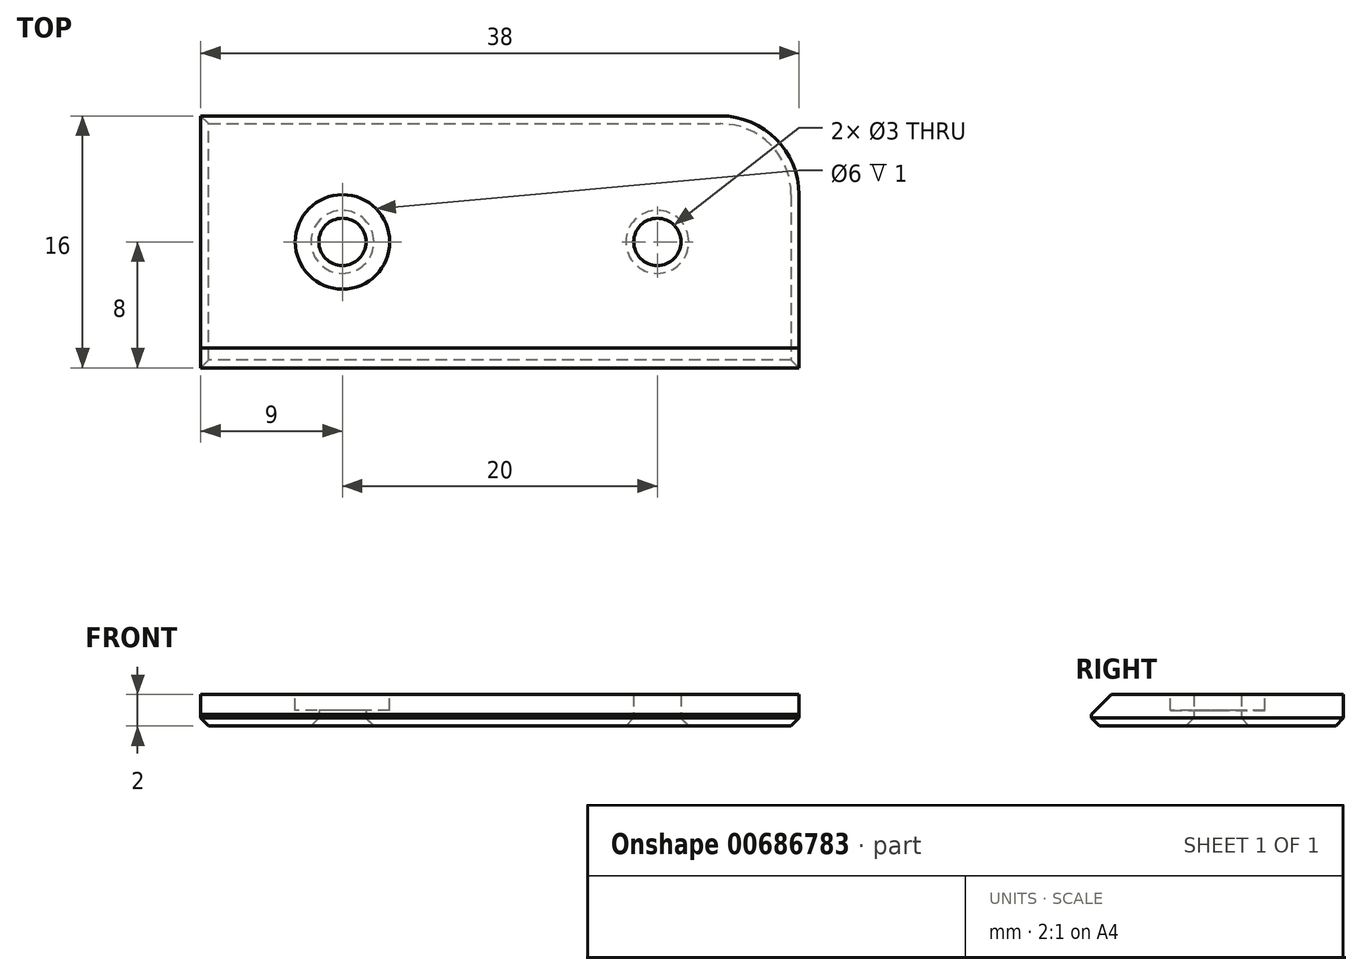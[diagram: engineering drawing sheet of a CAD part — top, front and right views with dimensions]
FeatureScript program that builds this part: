
annotation { "Feature Type Name" : "Feature", "Feature Type Description" : "" }
export const myFeature = defineFeature(function(context is Context, id is Id, definition is map)
    precondition{}
    {
        {
            var Q0;
            Q0=qCreatedBy(makeId("Top.planeOp"),FACE);
            var sketch = newSketch(context, id + "F0", { "sketchPlane" : qUnion([Q0])});
            skLineSegment(sketch, "E0.bottom", {"start": v(-19, 8) * mm, "end": v(19, 8) * mm});
            skLineSegment(sketch, "E0.top", {"start": v(-19, -8) * mm, "end": v(19, -8) * mm});
            skLineSegment(sketch, "E0.left", {"start": v(-19, 8) * mm, "end": v(-19, -8) * mm});
            skLineSegment(sketch, "E0.right", {"start": v(19, 8) * mm, "end": v(19, -8) * mm});
            skPoint(sketch, "E0.middle", {"position": v(0, 0) * mm});
            skCircle(sketch, "E1", {"center": v(-10, 0) * mm, "radius": 1.5 * mm});
            skPoint(sketch, "E1.centerSnap0", {"position": v(-19, 0) * mm});
            skCircle(sketch, "E2", {"center": v(10, 0) * mm, "radius": 1.5 * mm});
            skSolve(sketch);
        }
        {
            var Q0;
            Q0 = qSketchRegion(id + "F0", true);
            extrude(context, id + "F1", {"entities" : qUnion([Q0]), "depth" : 2 * mm, "offsetDistance" : 25 * mm});
        }
        {
            var Q0;
            Q0=makeQuery(id+"F1.opExtrude","CAP_EDGE",EDGE,{"disambiguationData":[OSD([sQuery(id+"F0.wireOp",EDGE,"E0.top")])],"isStart":false});
            chamfer(context, id + "F2", {"entities" : qUnion([Q0]), "width" : 1.25 * mm, "tangentPropagation" : true});
        }
        {
            var Q0;
            Q0=makeQuery(id+"F1.opExtrude","CAP_FACE",FACE,{"disambiguationData":[OSD([sQuery(id+"F0.wireOp",EDGE,"E0.bottom"),sQuery(id+"F0.wireOp",EDGE,"E0.top"),sQuery(id+"F0.wireOp",EDGE,"E0.left"),sQuery(id+"F0.wireOp",EDGE,"E0.right"),sQuery(id+"F0.wireOp",EDGE,"E1"),sQuery(id+"F0.wireOp",EDGE,"E2")])],"isStart":false});
            var sketch = newSketch(context, id + "F3", { "sketchPlane" : qUnion([Q0])});
            skCircle(sketch, "E3", {"center": v(-10, 0) * mm, "radius": 3 * mm});
            skSolve(sketch);
        }
        {
            var Q0;
            Q0=makeQuery(id+"F1.opExtrude","SWEPT_EDGE",EDGE,{"disambiguationData":[OSD([sQuery(id+"F0.wireOp",EDGE,"E0.bottom"),sQuery(id+"F0.wireOp",EDGE,"E0.right")])]});
            fillet(context, id + "F4", {"entities" : qUnion([Q0]), "radius" : 5 * mm, "tangentPropagation" : true, "allowEdgeOverflow" : false});
        }
        {
            var Q0;
            Q0=makeQuery(id+"F3.imprint","IMPRINT",FACE,{"disambiguationData":[TD([[makeQuery(id+"F3.imprint","IMPRINT",EDGE,{"derivedFrom":sQuery(id+"F3.wireOp",EDGE,"E3")}),1.0]])]});
            extrude(context, id + "F5", {"entities" : qUnion([Q0]), "operationType" : NewBodyOperationType.REMOVE, "oppositeDirection" : true, "depth" : 1 * mm, "offsetDistance" : 25 * mm});
        }
        {
            var Q0;
            Q0=makeQuery(id+"F1.opExtrude","CAP_FACE",FACE,{"disambiguationData":[OSD([sQuery(id+"F0.wireOp",EDGE,"E0.bottom"),sQuery(id+"F0.wireOp",EDGE,"E0.top"),sQuery(id+"F0.wireOp",EDGE,"E0.left"),sQuery(id+"F0.wireOp",EDGE,"E0.right"),sQuery(id+"F0.wireOp",EDGE,"E1"),sQuery(id+"F0.wireOp",EDGE,"E2")])],"isStart":true});
            chamfer(context, id + "F6", {"entities" : qUnion([Q0]), "width" : .5 * mm, "tangentPropagation" : true});
        }
    });
